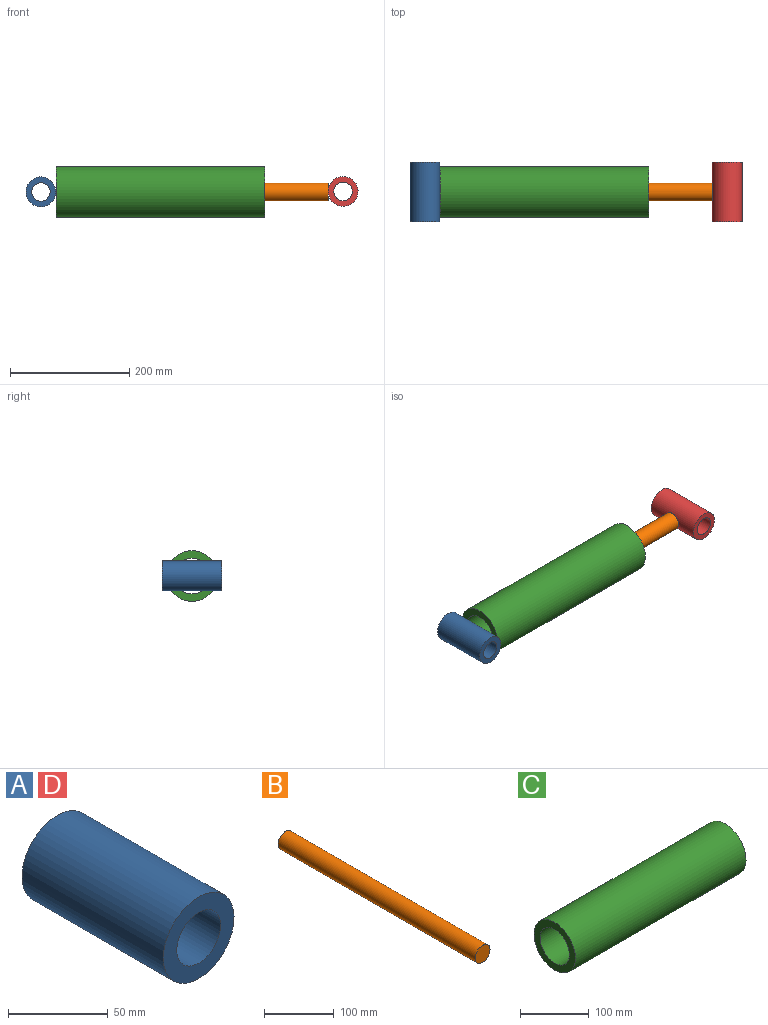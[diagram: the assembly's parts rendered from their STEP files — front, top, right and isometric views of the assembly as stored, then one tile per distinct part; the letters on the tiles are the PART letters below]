
ASSEMBLY  parts=4 mates=1
PART A: 4 faces, bbox 50x100x50 mm
  f0: cylinder r=15.5mm len=100mm, axis (0,1,0), area 9738.9mm2, adj f2,f3
  f1: cylinder r=25mm len=100mm, axis (0,1,0), area 15708mm2, adj f2,f3
  f2: plane 50x50mm, normal (0,-1,0), area 1208.7mm2, adj f0,f1
  f3: plane 50x50mm, normal (0,1,0), area 1208.7mm2, adj f0,f1
PART B: 3 faces, bbox 30x400x30 mm
  f0: cylinder r=15mm len=400mm, axis (0,1,0), area 37699.1mm2, adj f1,f2
  f1: plane 30x30mm, normal (0,-1,0), area 706.9mm2, adj f0
  f2: plane 30x30mm, normal (0,1,0), area 706.9mm2, adj f0
PART C: 4 faces, bbox 350x85x85 mm
  f0: plane 85x85mm, normal (-1,0,0), area 2847.1mm2, adj f1,f3
  f1: cylinder r=42.5mm len=350mm, axis (-1,0,0), area 93462.4mm2, adj f0,f2
  f2: plane 85x85mm, normal (1,0,0), area 2847.1mm2, adj f1,f3
  f3: cylinder r=30mm len=350mm, axis (-1,0,0), area 65973.4mm2, adj f0,f2
PART D: same geometry as A
PLACE A t=(-364.29,50,103.78)mm
PLACE B rot(axis=(0,0,1),90deg) t=(-282.78,0,103.51)mm
PLACE C t=(-229.36,0,53.51)mm
PLACE D t=(142.4,50,104.58)mm
MATE slider B.f0 <-> C.f1  axis (-1,0,0) through (-82.78,0,103.51)mm
